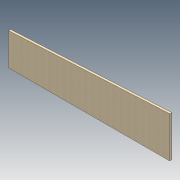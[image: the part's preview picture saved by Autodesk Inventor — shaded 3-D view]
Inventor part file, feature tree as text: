
AUTODESK INVENTOR PART (.ipt)
format: ipt  version: 2012 (Build 160160000, 160)  size: 74,240 bytes
history: native  units: in
note: dims shown in document units (in); Inventor stores cm internally (conversion verified against a paired STEP export)
features: extrude x1, sketch x1
ambient origin geometry x8: Origin, YZ Plane, XZ Plane, XY Plane, X Axis, Y Axis, Z Axis, Center Point
bodies: Solid1 (feature_tree)
feature tree (2):
  extrude  "Extrusion1"  Depth=7.5in
  sketch  "Sketch1"  dims[d0=37.5in d5=7.5in d6=0.5in d7=0.0in d9=9.5in]
